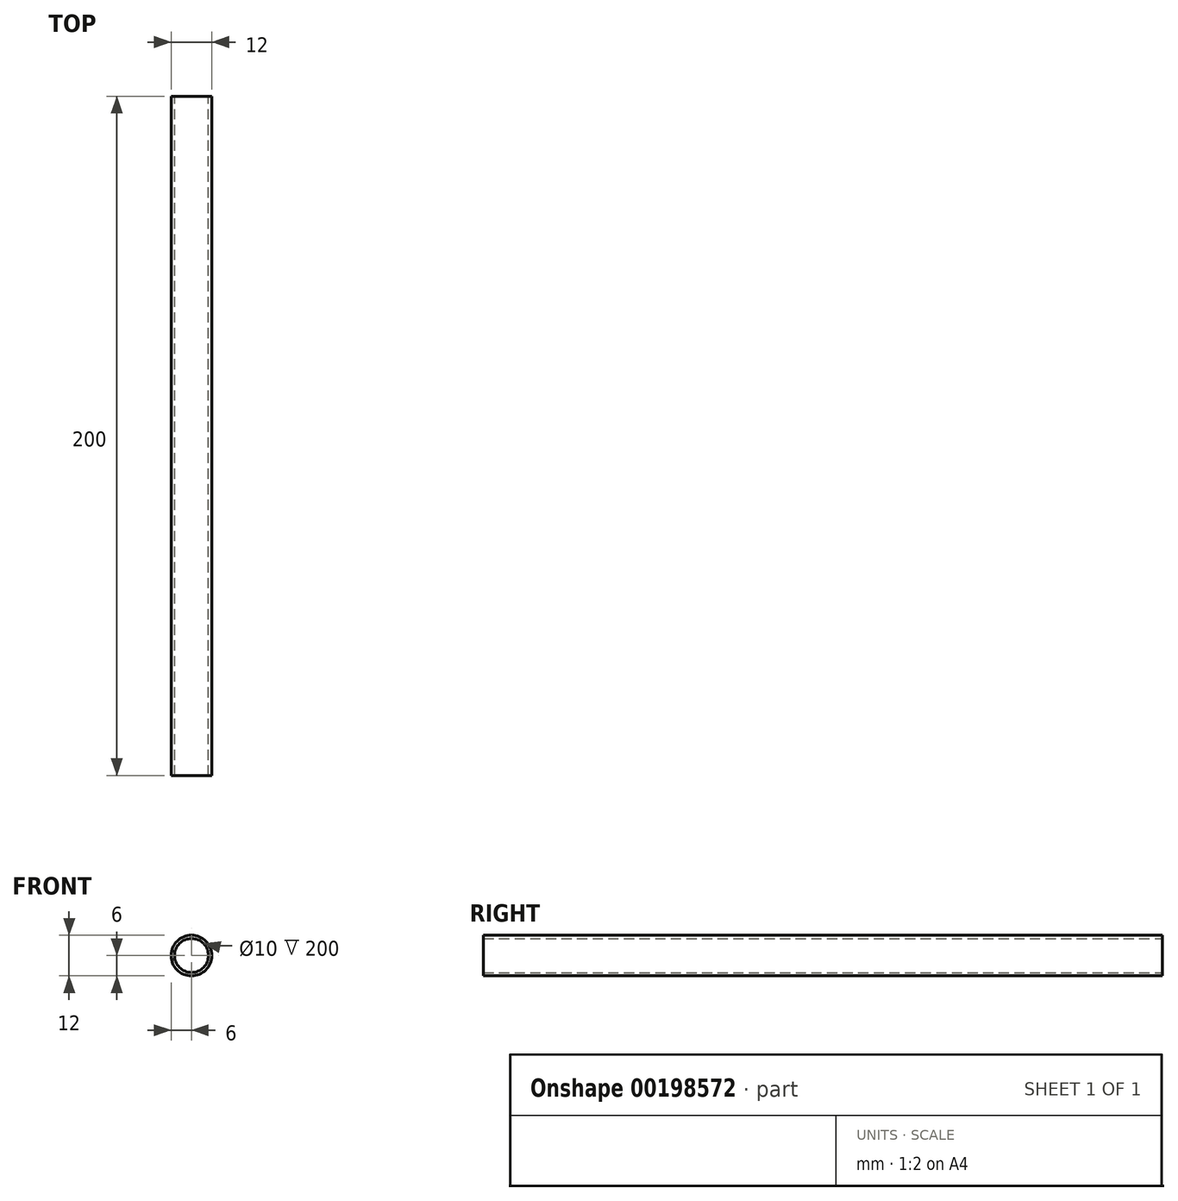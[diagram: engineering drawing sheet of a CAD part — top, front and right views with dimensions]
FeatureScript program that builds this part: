
annotation { "Feature Type Name" : "Feature", "Feature Type Description" : "" }
export const myFeature = defineFeature(function(context is Context, id is Id, definition is map)
    precondition{}
    {
        {
            var Q0;
            Q0=qCreatedBy(makeId("Front.planeOp"),FACE);
            var sketch = newSketch(context, id + "F0", { "sketchPlane" : qUnion([Q0])});
            skCircle(sketch, "E0", {"center": v(0, 0) * mm, "radius": 5 * mm});
            skCircle(sketch, "E1", {"center": v(0, 0) * mm, "radius": 6 * mm});
            skSolve(sketch);
        }
        {
            assignVariable(context, id + "F1", {"name" : "pipe_length", "anyValue" : 200});
        }
        {
            var Q0;
            Q0=makeQuery(id+"F0.imprint","IMPRINT",FACE,{"disambiguationData":[TD([[makeQuery(id+"F0.imprint","IMPRINT",EDGE,{"derivedFrom":sQuery(id+"F0.wireOp",EDGE,"E0")}),-1.0]])]});
            extrude(context, id + "F2", {"entities" : qUnion([Q0]), "depth" : (getVariable(context, 'pipe_length')) * mm});
        }
    });
